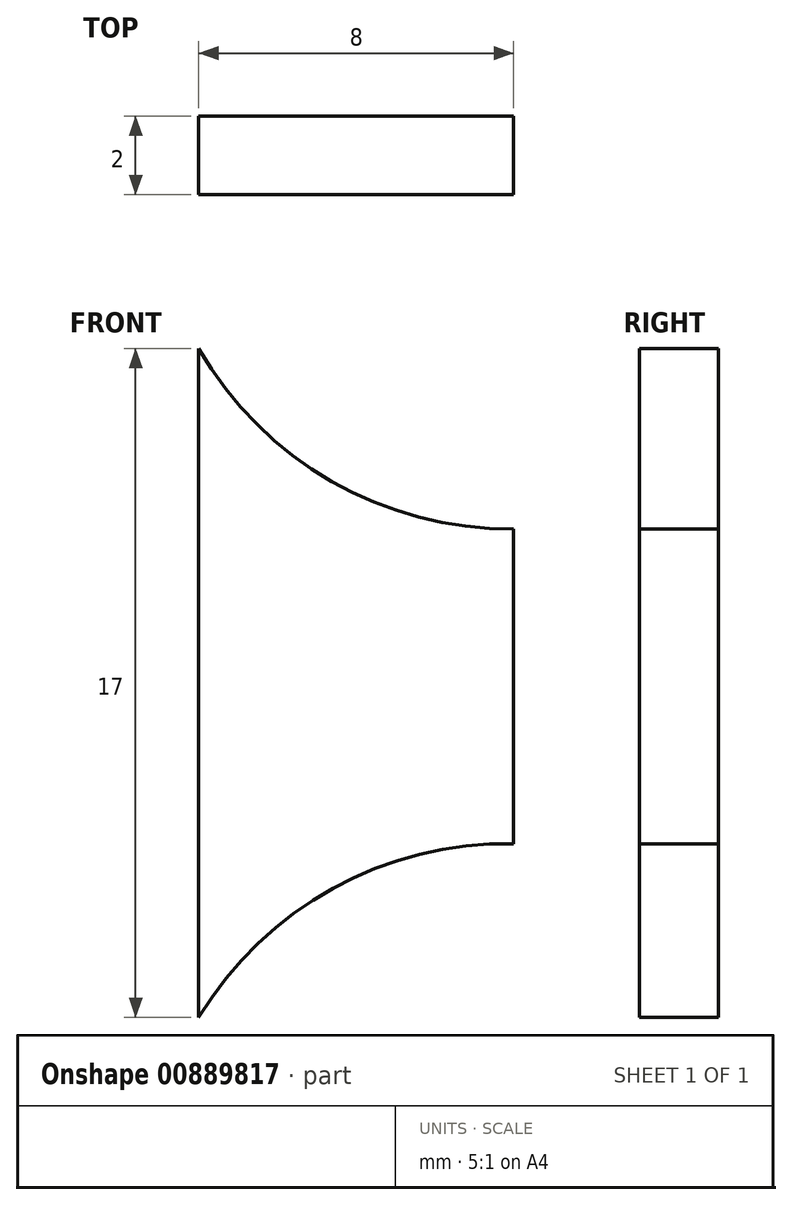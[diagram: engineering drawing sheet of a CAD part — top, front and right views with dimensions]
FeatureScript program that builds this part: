
annotation { "Feature Type Name" : "Feature", "Feature Type Description" : "" }
export const myFeature = defineFeature(function(context is Context, id is Id, definition is map)
    precondition{}
    {
        {
            var Q0;
            Q0=qCreatedBy(makeId("Front.planeOp"),FACE);
            var sketch = newSketch(context, id + "F0", { "sketchPlane" : qUnion([Q0])});
            skLineSegment(sketch, "E0", {"start": v(0, 0) * mm, "end": v(0, 17) * mm});
            skLineSegment(sketch, "E1", {"start": v(0, 0) * mm, "end": v(0, 8.5) * mm});
            skLineSegment(sketch, "E2", {"start": v(8, 8.41) * mm, "end": v(8, 12.41) * mm});
            skLineSegment(sketch, "E3", {"start": v(8, 8.41) * mm, "end": v(8, 4.41) * mm});
            skArc(sketch, "E4", {"start": v(8, 4.41) * mm, "mid": v(3.4, 3.28) * mm, "end": v(0, 0) * mm});
            skArc(sketch, "E5", {"start": v(0, 17) * mm, "mid": v(3.38, 13.62) * mm, "end": v(8, 12.41) * mm});
            skLineSegment(sketch, "E6", {"start": v(0, 8.5) * mm, "end": v(8, 8.41) * mm});
            skSolve(sketch);
        }
        {
            var Q0;
            Q0=makeQuery(id+"F0.imprint","IMPRINT",FACE,{"disambiguationData":[TD([[makeQuery(id+"F0.imprint","IMPRINT",EDGE,{"derivedFrom":sQuery(id+"F0.wireOp",EDGE,"E0")}),-1.0]])]});
            var Q1;
            Q1=makeQuery(id+"F0.imprint","IMPRINT",FACE,{"disambiguationData":[TD([[makeQuery(id+"F0.imprint","IMPRINT",EDGE,{"derivedFrom":sQuery(id+"F0.wireOp",EDGE,"E1")}),-1.0]])]});
            extrude(context, id + "F1", {"entities" : qUnion([Q0, Q1]), "depth" : 2 * mm, "offsetDistance" : 25 * mm});
        }
    });
